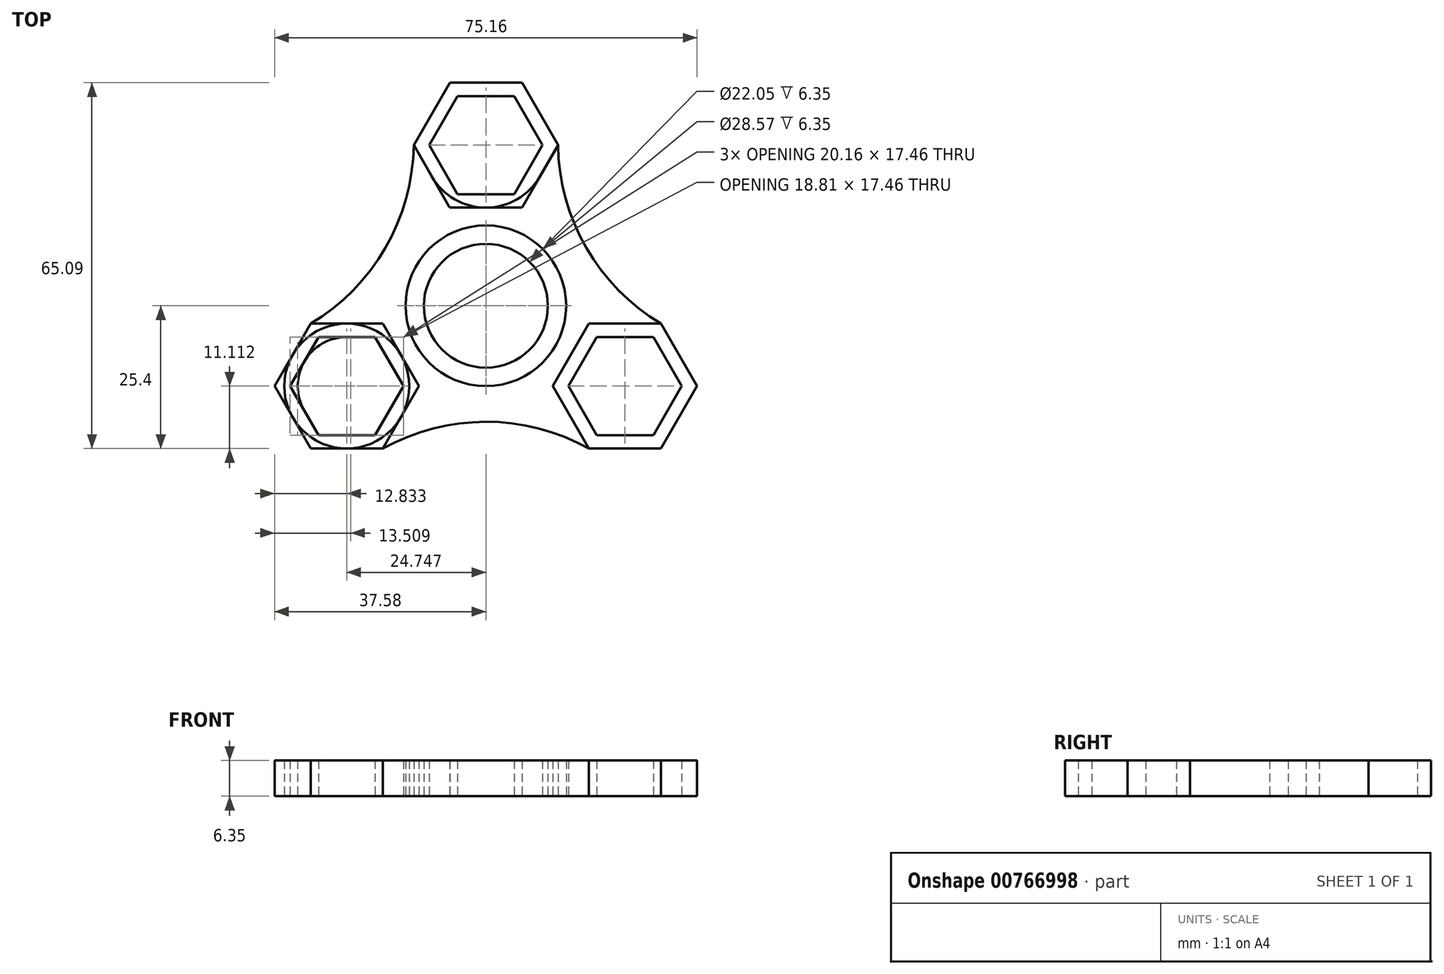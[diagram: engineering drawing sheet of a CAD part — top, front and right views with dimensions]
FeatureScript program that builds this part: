
annotation { "Feature Type Name" : "Feature", "Feature Type Description" : "" }
export const myFeature = defineFeature(function(context is Context, id is Id, definition is map)
    precondition{}
    {
        {
            var Q0;
            Q0=qCreatedBy(makeId("Top.planeOp"),FACE);
            var sketch = newSketch(context, id + "F0", { "sketchPlane" : qUnion([Q0])});
            skCircle(sketch, "E0", {"center": v(0, 0) * mm, "radius": 11.02 * mm});
            skCircle(sketch, "E1", {"center": v(0, 0) * mm, "radius": 14.29 * mm});
            skCircle(sketch, "E2.cCircle", {"center": v(0, 28.58) * mm, "radius": 8.73 * mm, "construction": true});
            skLineSegment(sketch, "E2.0", {"start": v(5.04, 19.84) * mm, "end": v(-5.04, 19.84) * mm});
            skLineSegment(sketch, "E2.1", {"start": v(-5.04, 19.84) * mm, "end": v(-10.08, 28.57) * mm});
            skLineSegment(sketch, "E2.2", {"start": v(-10.08, 28.57) * mm, "end": v(-5.04, 37.3) * mm});
            skLineSegment(sketch, "E2.3", {"start": v(-5.04, 37.3) * mm, "end": v(5.04, 37.3) * mm});
            skLineSegment(sketch, "E2.4", {"start": v(5.04, 37.3) * mm, "end": v(10.08, 28.58) * mm});
            skLineSegment(sketch, "E2.5", {"start": v(10.08, 28.57) * mm, "end": v(5.04, 19.84) * mm});
            skPoint(sketch, "E2.0.midPoint", {"position": v(0, 19.84) * mm});
            skCircle(sketch, "E3.cCircle", {"center": v(0, 28.58) * mm, "radius": 11.11 * mm, "construction": true});
            skLineSegment(sketch, "E3.0", {"start": v(6.42, 39.69) * mm, "end": v(12.83, 28.57) * mm});
            skLineSegment(sketch, "E3.1", {"start": v(12.83, 28.57) * mm, "end": v(6.41, 17.46) * mm});
            skLineSegment(sketch, "E3.2", {"start": v(6.41, 17.46) * mm, "end": v(-6.42, 17.46) * mm});
            skLineSegment(sketch, "E3.3", {"start": v(-6.42, 17.46) * mm, "end": v(-12.83, 28.58) * mm});
            skLineSegment(sketch, "E3.4", {"start": v(-12.83, 28.58) * mm, "end": v(-6.41, 39.69) * mm});
            skLineSegment(sketch, "E3.5", {"start": v(-6.41, 39.69) * mm, "end": v(6.42, 39.69) * mm});
            skPoint(sketch, "E3.0.midPoint", {"position": v(9.63, 34.13) * mm});
            skPoint(sketch, "E4.1.0", {"position": v(-34.37, -8.73) * mm});
            skCircle(sketch, "E4.1.1", {"center": v(-24.75, -14.29) * mm, "radius": 8.73 * mm, "construction": true});
            skCircle(sketch, "E4.1.2", {"center": v(-24.75, -14.29) * mm, "radius": 11.11 * mm, "construction": true});
            skPoint(sketch, "E4.1.3", {"position": v(-17.19, -9.92) * mm});
            skLineSegment(sketch, "E4.1.4", {"start": v(-11.92, -14.3) * mm, "end": v(-18.34, -25.4) * mm});
            skLineSegment(sketch, "E4.1.5", {"start": v(-19.7, -5.56) * mm, "end": v(-14.66, -14.29) * mm});
            skLineSegment(sketch, "E4.1.6", {"start": v(-14.66, -14.29) * mm, "end": v(-19.7, -23.02) * mm});
            skLineSegment(sketch, "E4.1.7", {"start": v(-29.79, -23.02) * mm, "end": v(-34.83, -14.29) * mm});
            skLineSegment(sketch, "E4.1.8", {"start": v(-29.79, -5.56) * mm, "end": v(-19.7, -5.56) * mm});
            skLineSegment(sketch, "E4.1.9", {"start": v(-37.58, -14.28) * mm, "end": v(-31.16, -3.17) * mm});
            skLineSegment(sketch, "E4.1.10", {"start": v(-31.16, -3.17) * mm, "end": v(-18.33, -3.18) * mm});
            skLineSegment(sketch, "E4.1.11", {"start": v(-18.33, -3.18) * mm, "end": v(-11.92, -14.3) * mm});
            skLineSegment(sketch, "E4.1.12", {"start": v(-18.34, -25.4) * mm, "end": v(-31.17, -25.4) * mm});
            skLineSegment(sketch, "E4.1.13", {"start": v(-31.17, -25.4) * mm, "end": v(-37.58, -14.28) * mm});
            skLineSegment(sketch, "E4.1.14", {"start": v(-19.7, -23.02) * mm, "end": v(-29.79, -23.02) * mm});
            skLineSegment(sketch, "E4.1.15", {"start": v(-34.83, -14.29) * mm, "end": v(-29.79, -5.56) * mm});
            skPoint(sketch, "E4.2.0", {"position": v(24.74, -25.4) * mm});
            skCircle(sketch, "E4.2.1", {"center": v(24.75, -14.29) * mm, "radius": 8.73 * mm, "construction": true});
            skCircle(sketch, "E4.2.2", {"center": v(24.75, -14.29) * mm, "radius": 11.11 * mm, "construction": true});
            skPoint(sketch, "E4.2.3", {"position": v(17.19, -9.92) * mm});
            skLineSegment(sketch, "E4.2.4", {"start": v(18.34, -3.17) * mm, "end": v(31.17, -3.18) * mm});
            skLineSegment(sketch, "E4.2.5", {"start": v(14.66, -14.29) * mm, "end": v(19.7, -5.56) * mm});
            skLineSegment(sketch, "E4.2.6", {"start": v(19.7, -5.56) * mm, "end": v(29.79, -5.56) * mm});
            skLineSegment(sketch, "E4.2.7", {"start": v(34.83, -14.29) * mm, "end": v(29.79, -23.02) * mm});
            skLineSegment(sketch, "E4.2.8", {"start": v(19.7, -23.02) * mm, "end": v(14.66, -14.29) * mm});
            skLineSegment(sketch, "E4.2.9", {"start": v(31.16, -25.4) * mm, "end": v(18.33, -25.4) * mm});
            skLineSegment(sketch, "E4.2.10", {"start": v(18.33, -25.4) * mm, "end": v(11.92, -14.28) * mm});
            skLineSegment(sketch, "E4.2.11", {"start": v(11.92, -14.28) * mm, "end": v(18.34, -3.17) * mm});
            skLineSegment(sketch, "E4.2.12", {"start": v(31.17, -3.18) * mm, "end": v(37.58, -14.3) * mm});
            skLineSegment(sketch, "E4.2.13", {"start": v(37.58, -14.3) * mm, "end": v(31.16, -25.4) * mm});
            skLineSegment(sketch, "E4.2.14", {"start": v(29.79, -5.56) * mm, "end": v(34.83, -14.29) * mm});
            skLineSegment(sketch, "E4.2.15", {"start": v(29.79, -23.02) * mm, "end": v(19.7, -23.02) * mm});
            skSolve(sketch);
        }
        {
            var Q0;
            Q0=qCreatedBy(makeId("Top.planeOp"),FACE);
            var sketch = newSketch(context, id + "F1", { "sketchPlane" : qUnion([Q0])});
            skLineSegment(sketch, "E5.0", {"start": v(19.7, -5.56) * mm, "end": v(29.79, -5.56) * mm});
            skLineSegment(sketch, "E5.1", {"start": v(-5.04, 37.3) * mm, "end": v(5.04, 37.3) * mm});
            skLineSegment(sketch, "E5.2", {"start": v(-10.08, 28.57) * mm, "end": v(-5.04, 37.3) * mm});
            skLineSegment(sketch, "E5.3", {"start": v(-12.83, 28.58) * mm, "end": v(-6.41, 39.69) * mm});
            skLineSegment(sketch, "E5.4", {"start": v(-5.04, 19.84) * mm, "end": v(-10.08, 28.57) * mm});
            skCircle(sketch, "E5.5", {"center": v(0, 0) * mm, "radius": 14.29 * mm});
            skCircle(sketch, "E5.6", {"center": v(0, 0) * mm, "radius": 11.02 * mm});
            skLineSegment(sketch, "E5.7", {"start": v(-6.42, 17.46) * mm, "end": v(-12.83, 28.58) * mm});
            skCircle(sketch, "E5.8", {"center": v(0, 28.58) * mm, "radius": 11.11 * mm});
            skLineSegment(sketch, "E5.9", {"start": v(34.83, -14.29) * mm, "end": v(29.79, -23.02) * mm});
            skLineSegment(sketch, "E5.10", {"start": v(10.08, 28.57) * mm, "end": v(5.04, 19.84) * mm});
            skLineSegment(sketch, "E5.11", {"start": v(-6.41, 39.69) * mm, "end": v(6.42, 39.69) * mm});
            skLineSegment(sketch, "E5.12", {"start": v(12.83, 28.57) * mm, "end": v(6.41, 17.46) * mm});
            skLineSegment(sketch, "E5.13", {"start": v(-31.17, -25.4) * mm, "end": v(-37.58, -14.28) * mm});
            skLineSegment(sketch, "E5.14", {"start": v(11.92, -14.28) * mm, "end": v(18.34, -3.17) * mm});
            skLineSegment(sketch, "E5.15", {"start": v(-14.66, -14.29) * mm, "end": v(-19.7, -23.02) * mm});
            skLineSegment(sketch, "E5.16", {"start": v(19.7, -23.02) * mm, "end": v(14.66, -14.29) * mm});
            skLineSegment(sketch, "E5.17", {"start": v(18.34, -3.17) * mm, "end": v(31.17, -3.18) * mm});
            skLineSegment(sketch, "E5.18", {"start": v(-19.7, -23.02) * mm, "end": v(-29.79, -23.02) * mm});
            skLineSegment(sketch, "E5.19", {"start": v(31.17, -3.18) * mm, "end": v(37.58, -14.3) * mm});
            skLineSegment(sketch, "E5.20", {"start": v(-31.16, -3.17) * mm, "end": v(-18.33, -3.18) * mm});
            skLineSegment(sketch, "E5.21", {"start": v(-29.79, -23.02) * mm, "end": v(-34.83, -14.29) * mm});
            skCircle(sketch, "E5.22", {"center": v(24.75, -14.29) * mm, "radius": 8.73 * mm});
            skCircle(sketch, "E5.23", {"center": v(-24.75, -14.29) * mm, "radius": 11.11 * mm});
            skLineSegment(sketch, "E5.24", {"start": v(37.58, -14.3) * mm, "end": v(31.16, -25.4) * mm});
            skLineSegment(sketch, "E5.25", {"start": v(-18.33, -3.18) * mm, "end": v(-11.92, -14.3) * mm});
            skCircle(sketch, "E5.26", {"center": v(24.75, -14.29) * mm, "radius": 11.11 * mm});
            skLineSegment(sketch, "E5.27", {"start": v(-29.79, -5.56) * mm, "end": v(-19.7, -5.56) * mm});
            skLineSegment(sketch, "E5.28", {"start": v(18.33, -25.4) * mm, "end": v(11.92, -14.28) * mm});
            skLineSegment(sketch, "E5.29", {"start": v(-11.92, -14.3) * mm, "end": v(-18.34, -25.4) * mm});
            skLineSegment(sketch, "E5.30", {"start": v(-18.34, -25.4) * mm, "end": v(-31.17, -25.4) * mm});
            skLineSegment(sketch, "E5.31", {"start": v(29.79, -5.56) * mm, "end": v(34.83, -14.29) * mm});
            skCircle(sketch, "E5.32", {"center": v(0, 28.58) * mm, "radius": 8.73 * mm});
            skLineSegment(sketch, "E5.33", {"start": v(6.42, 39.69) * mm, "end": v(12.83, 28.57) * mm});
            skCircle(sketch, "E5.34", {"center": v(-24.75, -14.29) * mm, "radius": 8.73 * mm});
            skLineSegment(sketch, "E5.35", {"start": v(14.66, -14.29) * mm, "end": v(19.7, -5.56) * mm});
            skLineSegment(sketch, "E5.36", {"start": v(-19.7, -5.56) * mm, "end": v(-14.66, -14.29) * mm});
            skArc(sketch, "E6", {"start": v(12.83, 28.57) * mm, "mid": v(17.87, 10.31) * mm, "end": v(31.17, -3.18) * mm});
            skArc(sketch, "E7", {"start": v(-31.16, -3.17) * mm, "mid": v(-17.87, 10.32) * mm, "end": v(-12.83, 28.58) * mm});
            skArc(sketch, "E8", {"start": v(18.33, -25.4) * mm, "mid": v(0, -20.64) * mm, "end": v(-18.34, -25.4) * mm});
            skSolve(sketch);
        }
        {
            var Q0;
            Q0=makeQuery(id+"F1.imprint","IMPRINT",FACE,{"disambiguationData":[TD([[makeQuery(id+"F1.imprint","IMPRINT",EDGE,{"derivedFrom":sQuery(id+"F1.wireOp",EDGE,"E5.5")}),-1.0]])]});
            var Q1;
            Q1=makeQuery(id+"F0.imprint","IMPRINT",FACE,{"disambiguationData":[TD([[makeQuery(id+"F0.imprint","IMPRINT",EDGE,{"derivedFrom":sQuery(id+"F0.wireOp",EDGE,"E2.0")}),1.0]])]});
            var Q2;
            Q2=makeQuery(id+"F0.imprint","IMPRINT",FACE,{"disambiguationData":[TD([[makeQuery(id+"F0.imprint","IMPRINT",EDGE,{"derivedFrom":sQuery(id+"F0.wireOp",EDGE,"E0")}),-1.0]])]});
            var Q3;
            Q3=makeQuery(id+"F0.imprint","IMPRINT",FACE,{"disambiguationData":[TD([[makeQuery(id+"F0.imprint","IMPRINT",EDGE,{"derivedFrom":sQuery(id+"F0.wireOp",EDGE,"E4.2.4")}),-1.0]])]});
            var Q4;
            {var subQ11=sQuery(id+"F1.wireOp",EDGE,"E5.36");var subQ12=sQuery(id+"F1.wireOp",EDGE,"E5.15");var subQ13=makeQuery(id+"F1.imprint","INTERSECT",VERTEX,{"derivedFrom":[subQ12,subQ11]});Q4=makeQuery(id+"F1.imprint","IMPRINT",FACE,{"disambiguationData":[TD([[makeQuery(id+"F1.imprint","IMPRINT",EDGE,{"disambiguationData":[TD([[subQ13,-1.0]])],"derivedFrom":subQ12}),1.0]])]});}
            var Q5;
            Q5=makeQuery(id+"F0.imprint","IMPRINT",FACE,{"disambiguationData":[TD([[makeQuery(id+"F0.imprint","IMPRINT",EDGE,{"derivedFrom":sQuery(id+"F0.wireOp",EDGE,"E4.1.4")}),-1.0]])]});
            extrude(context, id + "F2", {"entities" : qUnion([Q0, Q1, Q2, Q3, Q4, Q5]), "depth" : 6.35 * mm, "offsetDistance" : 25.4 * mm});
        }
    });
